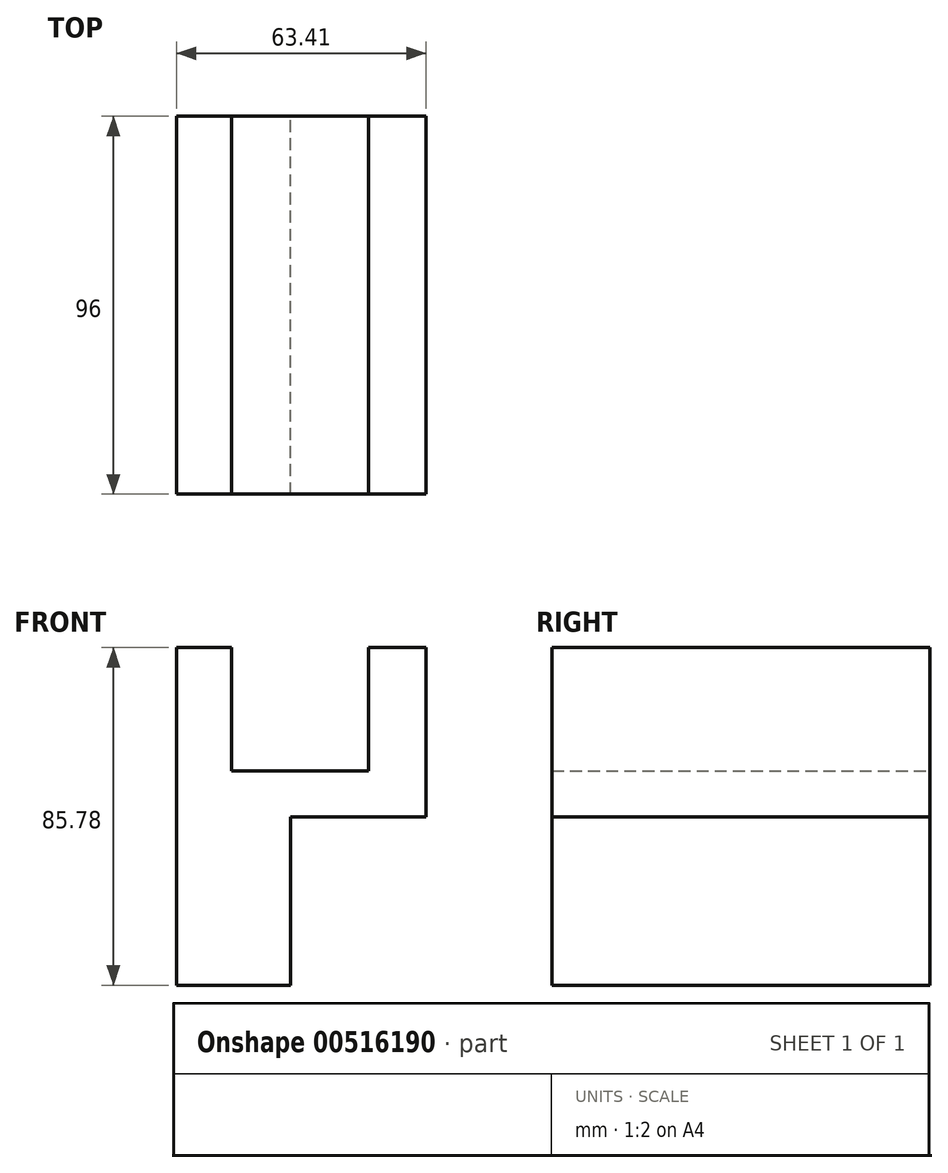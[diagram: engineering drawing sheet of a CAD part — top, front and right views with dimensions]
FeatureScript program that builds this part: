
annotation { "Feature Type Name" : "Feature", "Feature Type Description" : "" }
export const myFeature = defineFeature(function(context is Context, id is Id, definition is map)
    precondition{}
    {
        {
            var Q0;
            Q0=qCreatedBy(makeId("Front.planeOp"),FACE);
            var sketch = newSketch(context, id + "F0", { "sketchPlane" : qUnion([Q0])});
            skLineSegment(sketch, "E0", {"start": v(15, 0) * mm, "end": v(49.45, 0) * mm});
            skLineSegment(sketch, "E1", {"start": v(49.45, 0) * mm, "end": v(49.45, 43.04) * mm});
            skLineSegment(sketch, "E2", {"start": v(49.45, 43.04) * mm, "end": v(34.8, 43.04) * mm});
            skLineSegment(sketch, "E3", {"start": v(34.8, 43.04) * mm, "end": v(34.8, 11.68) * mm});
            skLineSegment(sketch, "E4", {"start": v(34.8, 11.68) * mm, "end": v(0, 11.68) * mm});
            skLineSegment(sketch, "E5", {"start": v(0, 11.68) * mm, "end": v(0, 43.04) * mm});
            skLineSegment(sketch, "E6", {"start": v(0, 43.04) * mm, "end": v(-13.96, 43.04) * mm});
            skLineSegment(sketch, "E7", {"start": v(-13.96, 43.04) * mm, "end": v(-13.96, -42.74) * mm});
            skLineSegment(sketch, "E8", {"start": v(-13.96, -42.74) * mm, "end": v(15, -42.74) * mm});
            skLineSegment(sketch, "E9", {"start": v(15, 0) * mm, "end": v(15, -42.74) * mm});
            skSolve(sketch);
        }
        {
            var Q0;
            Q0=makeQuery(id+"F0.imprint","IMPRINT",FACE,{"disambiguationData":[TD([[makeQuery(id+"F0.imprint","IMPRINT",EDGE,{"derivedFrom":sQuery(id+"F0.wireOp",EDGE,"E0")}),1.0]])]});
            extrude(context, id + "F1", {"entities" : qUnion([Q0]), "endBound" : BoundingType.SYMMETRIC, "depth" : 96 * mm, "offsetDistance" : 25 * mm});
        }
    });
